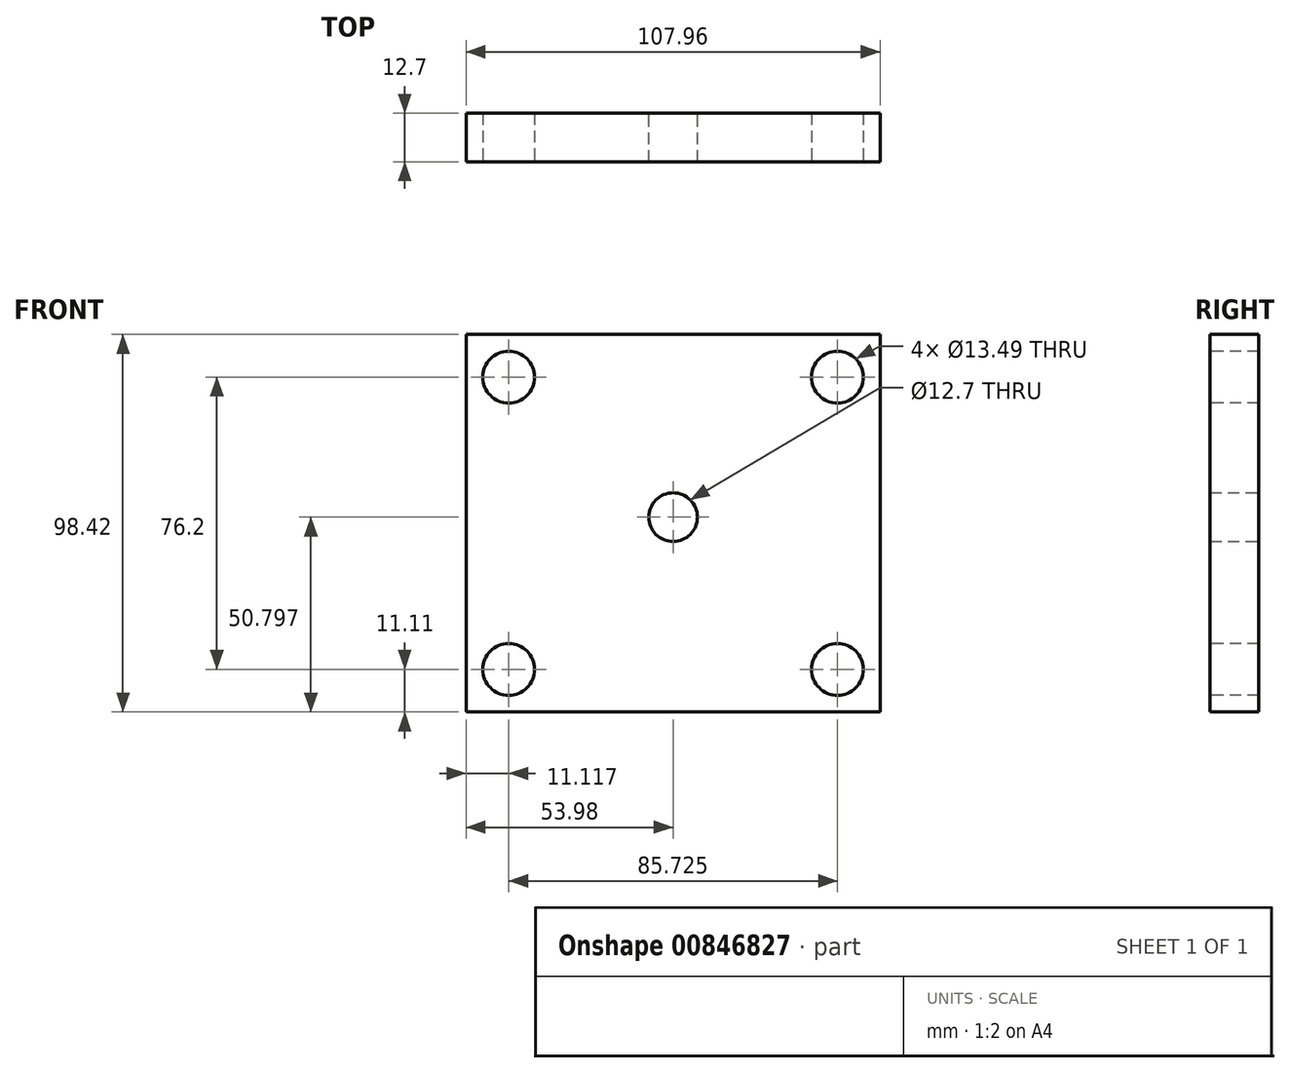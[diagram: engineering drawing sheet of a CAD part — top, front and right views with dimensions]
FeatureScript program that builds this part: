
annotation { "Feature Type Name" : "Feature", "Feature Type Description" : "" }
export const myFeature = defineFeature(function(context is Context, id is Id, definition is map)
    precondition{}
    {
        {
            var Q0;
            Q0=qCreatedBy(makeId("Front.planeOp"),FACE);
            var sketch = newSketch(context, id + "F0", { "sketchPlane" : qUnion([Q0])});
            skLineSegment(sketch, "E0.bottom", {"start": v(-53.98, 49.21) * mm, "end": v(53.98, 49.21) * mm});
            skLineSegment(sketch, "E0.top", {"start": v(-53.98, -49.21) * mm, "end": v(53.97, -49.21) * mm});
            skLineSegment(sketch, "E0.left", {"start": v(-53.98, 49.21) * mm, "end": v(-53.98, -49.21) * mm});
            skLineSegment(sketch, "E0.right", {"start": v(53.98, 49.21) * mm, "end": v(53.97, -49.21) * mm});
            skLineSegment(sketch, "E1.bottom", {"start": v(-42.86, 38.1) * mm, "end": v(42.86, 38.1) * mm, "construction": true});
            skLineSegment(sketch, "E1.top", {"start": v(-42.86, -38.1) * mm, "end": v(42.86, -38.1) * mm, "construction": true});
            skLineSegment(sketch, "E1.left", {"start": v(-42.86, 38.1) * mm, "end": v(-42.86, -38.1) * mm, "construction": true});
            skLineSegment(sketch, "E1.right", {"start": v(42.86, 38.1) * mm, "end": v(42.86, -38.1) * mm, "construction": true});
            skLineSegment(sketch, "E2", {"start": v(-42.86, -38.1) * mm, "end": v(42.86, 38.1) * mm, "construction": true});
            skLineSegment(sketch, "E3", {"start": v(-53.98, 49.21) * mm, "end": v(53.97, -49.21) * mm, "construction": true});
            skPoint(sketch, "E4", {"position": v(-42.86, 38.1) * mm});
            skPoint(sketch, "E5", {"position": v(42.86, 38.1) * mm});
            skPoint(sketch, "E6", {"position": v(42.86, -38.1) * mm});
            skPoint(sketch, "E7", {"position": v(-42.86, -38.1) * mm});
            skCircle(sketch, "E8", {"center": v(0, 1.59) * mm, "radius": 6.35 * mm});
            skSolve(sketch);
        }
        {
            var Q0;
            Q0 = qSketchRegion(id + "F0", true);
            extrude(context, id + "F1", {"entities" : qUnion([Q0]), "depth" : 12.7 * mm, "offsetDistance" : 25.4 * mm});
        }
        {
            var Q0;
            Q0=sQuery(id+"F0.wireOp",VERTEX,"E4");
            var Q1;
            Q1=sQuery(id+"F0.wireOp",VERTEX,"E5");
            var Q2;
            Q2=sQuery(id+"F0.wireOp",VERTEX,"E6");
            var Q3;
            Q3=sQuery(id+"F0.wireOp",VERTEX,"E7");
            var Q4;
            Q4=makeQuery(id+"F1.opExtrude","SWEPT_BODY",BODY,{"disambiguationData":[OSD([sQuery(id+"F0.wireOp",EDGE,"E0.bottom"),sQuery(id+"F0.wireOp",EDGE,"E0.top"),sQuery(id+"F0.wireOp",EDGE,"E0.left"),sQuery(id+"F0.wireOp",EDGE,"E0.right")])]});
            hole(context, id + "F2", {"style" : HoleStyle.SIMPLE, "endStyle" : HoleEndStyle.THROUGH, "oppositeDirection" : true, "standardTappedOrClearance" : lookupTablePath({ "fit" : "Free", "standard" : "ANSI", "size" : "1/2", "type" : "Clearance" }), "standardBlindInLast" : lookupTablePath({ "fit" : "Free", "standard" : "ANSI", "engagement" : "75%", "pitch" : "13 tpi", "size" : "1/2", "type" : "Clearance & tapped" }), "holeDiameter" : 13.5 * mm, "majorDiameter" : 12.7 * mm, "tappedDepth" : 9.52 * mm, "tapClearance" : 3, "locations" : qUnion([Q0, Q1, Q2, Q3]), "scope" : qUnion([Q4]), "startStyle" : HoleStartStyle.SKETCH});
        }
    });
